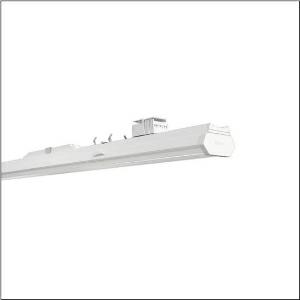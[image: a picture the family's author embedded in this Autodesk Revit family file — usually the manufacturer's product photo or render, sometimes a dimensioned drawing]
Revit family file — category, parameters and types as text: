
# Revit family: licross_r__11_protected_extreme_mo_51ts12dn48xfe_f3b0
name_source: partatom
category: Lighting Fixtures
units: mm (PartAtom-declared; Revit-internal decimal feet)

## family parameters
Cut with Voids When Loaded = No
Host = Face
Light Source = No
Part Type = Normal
Room Calculation Point = No
Round Connector Dimension = Use Diameter
Shared = No

## types (1)
- --- (1 x LED, 8470 lm, 56.2 W, 4000K)
    Apparent Load = 56 VA
    CIE Flux Codes = 54 82 95 97 100
    Color Rendering = 80
    Color Temperature = 4000K
    Default Elevation = 1800 mm
    Description = Licross® 11 Protected extreme MOluminaire insert, length: 1.500mm, width: 90mm, height: 101mm, LED rated luminous flux: 8.470lm, light colour: 840, control gear: DALI 2, control gear: ECG DALI, with plug, 5-pole, with phase selection, mains connection: 220..240V, AC, 50/60Hz, halogen-free wiring, primary optical cover: cover, of PMMA, light emission: direct with ceiling illumination distribution, protection rating (complete): IP50, insulation class (complete): insulation class I (protective earthing), certification: CE, ENEC, VDE, protection symbol: D if used in an environment with non-conductive dust loads with corresponding accessories, permissible ambient temperature for indoor applications: -25..+50°C, reducing of maximum allowable ambient temperature of 5°C with ceiling mounting, corresponds to IFS (International Featured Standards) requirements for safety and quality in the food industry, packaging unit: 1 piece
    Height = 92 mm
    Lamp = 1 x LED
    Lamp Light Flux = 8470 lm
    Lamp Power = 56.2 W
    Lamp count = 1
    Length = 1500 mm
    Luminous efficacy = 151 lm/W
    Manufacturer = Siteco
    ModVariant = No
    Model = 51TS12DN48XFE
    Mounting Place = Ceiling
    Mounting Type = Pendant
    Number of Poles = 1
    OnlyDefault = Yes
    Power Factor = 1
    Product Name = Licross® 11 Protected extreme MO
    Product group = luminaire insert
    ProductGroupID = 902
    Protection Class = Protection class I
    Protection Degree = IP 50
    RLX_Detail_Level = 1
    RlxData = <blob elided: 23889 chars, md5=1903b777>
    Socket = socket
    Standby Power = 0 W
    System Light Flux = 8470 lm
    System Power = 56 W
    Type Comments = factory setting: luminous flux: 100 % | dim-lin: 254 | 370 mA
    Type Image = l_1256145.jpg
    URL = http://relux.com
    VarID = @adj_132834
    Voltage = 0 V
    Weight = 0.00 kg
    Width = 88 mm

## geometry (parser evidence)
native form markers: Blend x4, Sweep x12
no freeform markers — native parametric forms only
